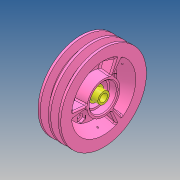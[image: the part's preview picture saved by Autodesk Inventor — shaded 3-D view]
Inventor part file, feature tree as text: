
AUTODESK INVENTOR PART (.ipt)
format: ipt  version: 2017 (Build 210142000, 142)  size: 676,864 bytes
history: native  units: mm
features: revolve x5, sketch x4, extrude x3, other x2, chamfer x2, plane x2, fillet x1, pattern_circular x1, projected_geometry x1
ambient origin geometry x8: Origin, YZ Plane, XZ Plane, XY Plane, X Axis, Y Axis, Z Axis, Center Point
bodies: Body1 (feature_tree), Body2 (feature_tree)
feature tree (21):
  other  "Sólido1"
  sketch  "Boceto1"  dims[d0=8.0mm d1=28.5mm]
  revolve  "Revolución1"  [1 undecoded]
  sketch  "Boceto2"  dims[d2=24.5mm d3=6.0mm]
  extrude  "Extrusión1"  Depth=6.0mm
  chamfer  "Chaflán1"  Distance=20.0mm
  extrude  "Extrusión2"  TaperAngle=90.0deg  [1 undecoded]
  extrude  "Extrusión3"  Depth=8.0mm
  chamfer  "Chaflán2"  Distance=3.0mm
  plane  "Plano de trabajo1"
  revolve  "Revolución3"  [1 undecoded]
  fillet  "Empalme1"  Radius=10.0mm
  plane  "Plano de trabajo2"
  revolve  "Revolución4"  [1 undecoded]
  revolve  "Revolución5"  [1 undecoded]
  pattern_circular  "Patrón circular1"  [2 undecoded]
  revolve  "Revolución2"  [1 undecoded]
  other  "espaciador"
  sketch  "Boceto3"  dims[d4=4.0mm]
  sketch  "Boceto4"  dims[d5=90.0mm d6=20.0mm d7=2.5mm d8=90.0deg d10=9.0mm d11=3.0mm d13=47.0mm d14=10.0mm d15=0.0mm d16=10.0mm d17=0.0mm d18=8.0mm d20=2.094395mm d24=44.5mm d25=44.0mm d26=8.0mm d27=12.0mm d28=16.0mm d29=8.0mm d30=90.0deg d31=24.0mm d32=30.0mm d33=17.790202mm d34=8.281806mm d35=3.0mm d36=0.0mm d37=60.0deg d38=2.094395mm d39=1.5mm d40=30.0mm d41=360.0deg d43=60.0deg d44=1.5mm d45=2.094395mm d46=1.0mm d47=2.0mm d48=45.0deg d49=0.4mm d50=2.0mm d51=45.0deg d52=4.0mm d53=70.0mm d54=3.0mm d55=90.0deg d56=120.0deg]
  projected_geometry  "Contorno proyectado1"
note: 8 required parameter values undecoded (feature->parameter linkage not recoverable at this tier; creation-order binding heuristic only, values carry confidence <= 0.55)